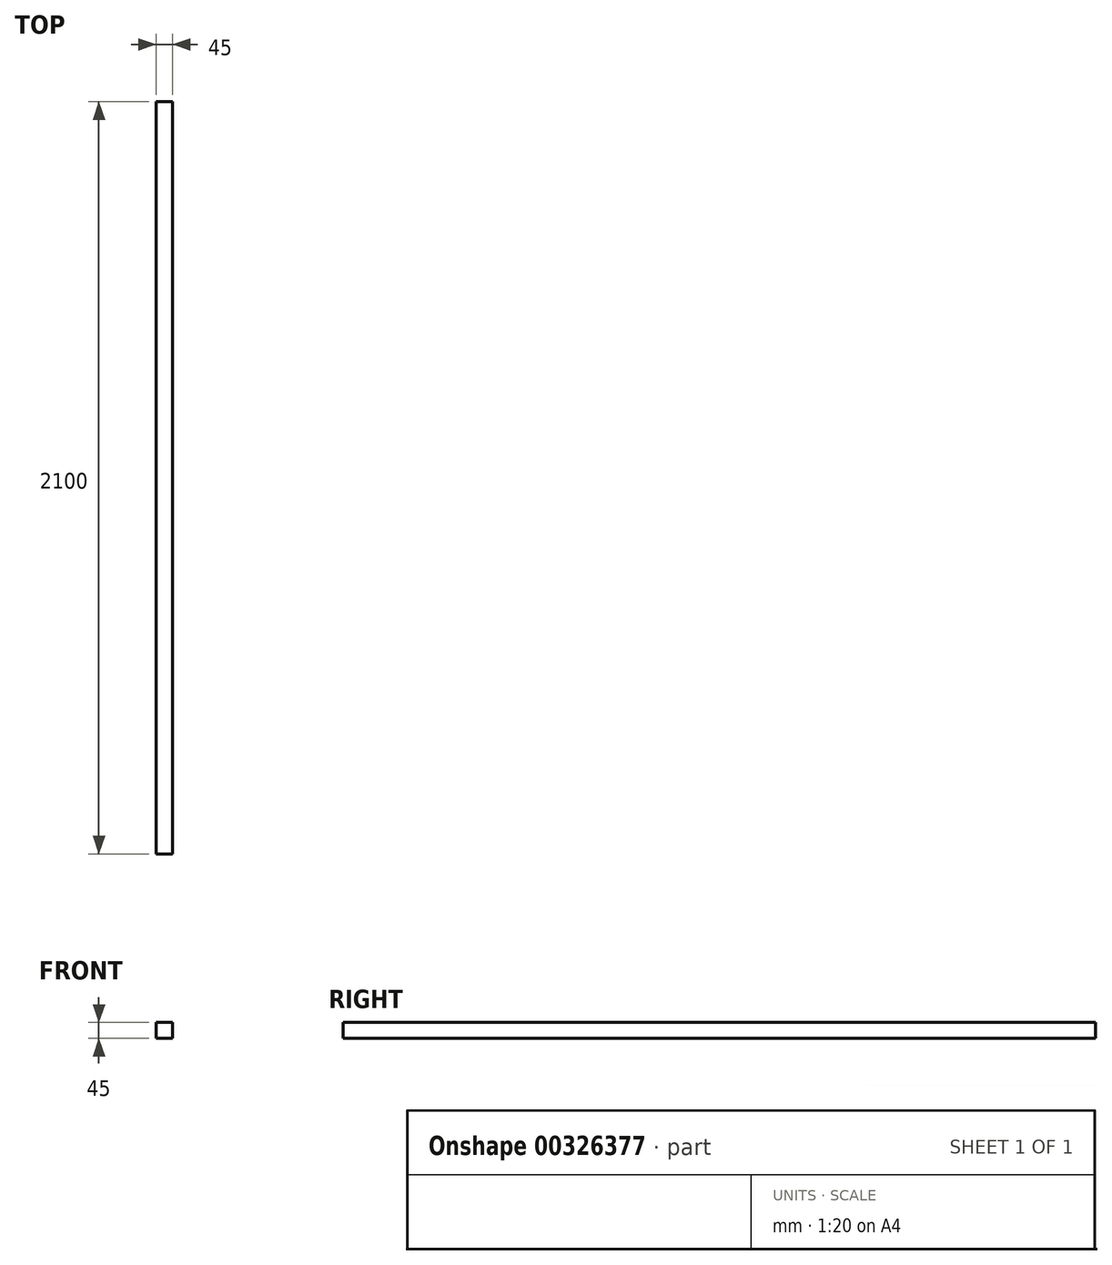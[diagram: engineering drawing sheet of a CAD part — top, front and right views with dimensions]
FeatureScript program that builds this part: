
annotation { "Feature Type Name" : "Feature", "Feature Type Description" : "" }
export const myFeature = defineFeature(function(context is Context, id is Id, definition is map)
    precondition{}
    {
        {
            var Q0;
            Q0=qCreatedBy(makeId("Front.planeOp"),FACE);
            var sketch = newSketch(context, id + "F0", { "sketchPlane" : qUnion([Q0])});
            skLineSegment(sketch, "E0.bottom", {"start": v(0, 0) * mm, "end": v(45, 0) * mm});
            skLineSegment(sketch, "E0.top", {"start": v(0, 45) * mm, "end": v(45, 45) * mm});
            skLineSegment(sketch, "E0.left", {"start": v(0, 0) * mm, "end": v(0, 45) * mm});
            skLineSegment(sketch, "E0.right", {"start": v(45, 0) * mm, "end": v(45, 45) * mm});
            skSolve(sketch);
        }
        {
            var Q0;
            Q0=makeQuery(id+"F0.imprint","IMPRINT",FACE,{"disambiguationData":[TD([[makeQuery(id+"F0.imprint","IMPRINT",EDGE,{"derivedFrom":sQuery(id+"F0.wireOp",EDGE,"E0.bottom")}),1.0]])]});
            extrude(context, id + "F1", {"entities" : qUnion([Q0]), "depth" : 2100 * mm});
        }
    });
